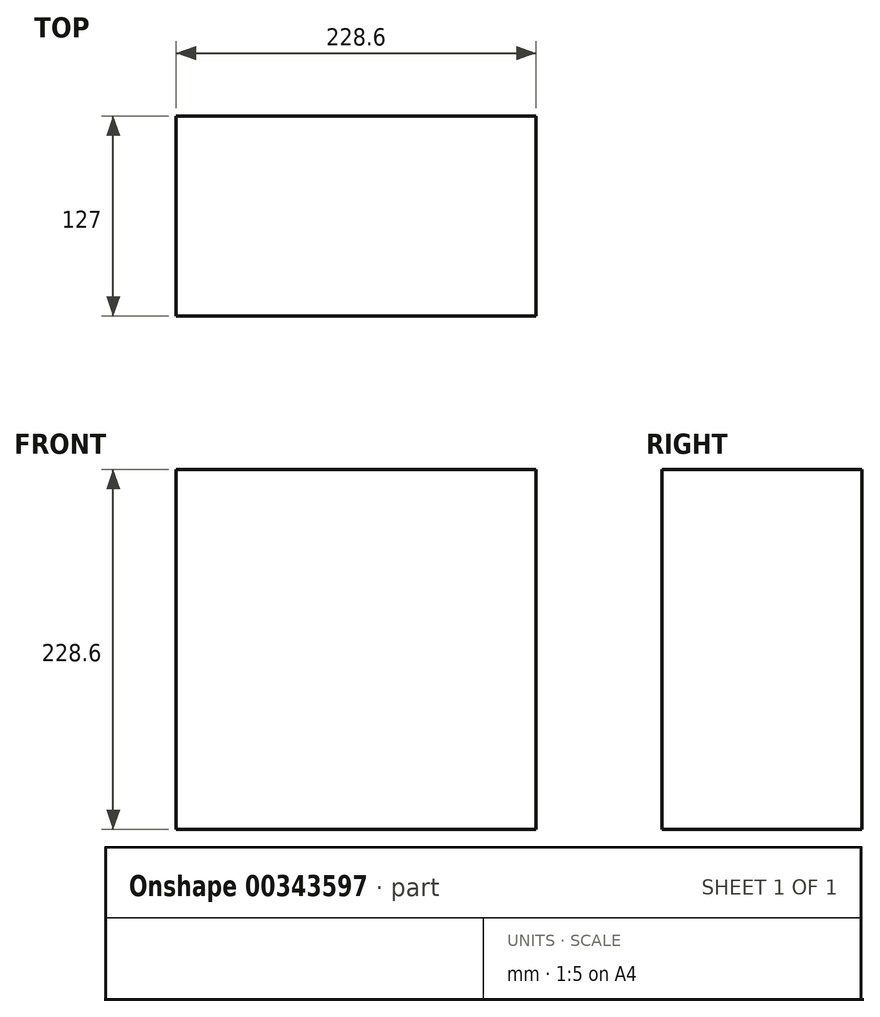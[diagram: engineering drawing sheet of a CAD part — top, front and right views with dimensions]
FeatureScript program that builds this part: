
annotation { "Feature Type Name" : "Feature", "Feature Type Description" : "" }
export const myFeature = defineFeature(function(context is Context, id is Id, definition is map)
    precondition{}
    {
        {
            var Q0;
            Q0=qCreatedBy(makeId("Front.planeOp"),FACE);
            var sketch = newSketch(context, id + "F0", { "sketchPlane" : qUnion([Q0])});
            skLineSegment(sketch, "E0.bottom", {"start": v(-112.98, 114.28) * mm, "end": v(115.62, 114.28) * mm});
            skLineSegment(sketch, "E0.top", {"start": v(-112.98, -114.32) * mm, "end": v(115.62, -114.32) * mm});
            skLineSegment(sketch, "E0.left", {"start": v(-112.98, 114.28) * mm, "end": v(-112.98, -114.32) * mm});
            skLineSegment(sketch, "E0.right", {"start": v(115.62, 114.28) * mm, "end": v(115.62, -114.32) * mm});
            skSolve(sketch);
        }
        {
            var Q0;
            Q0=makeQuery(id+"F0.imprint","IMPRINT",FACE,{"disambiguationData":[TD([[makeQuery(id+"F0.imprint","IMPRINT",EDGE,{"derivedFrom":sQuery(id+"F0.wireOp",EDGE,"E0.bottom")}),-1.0]])]});
            extrude(context, id + "F1", {"entities" : qUnion([Q0]), "depth" : 127 * mm});
        }
    });
